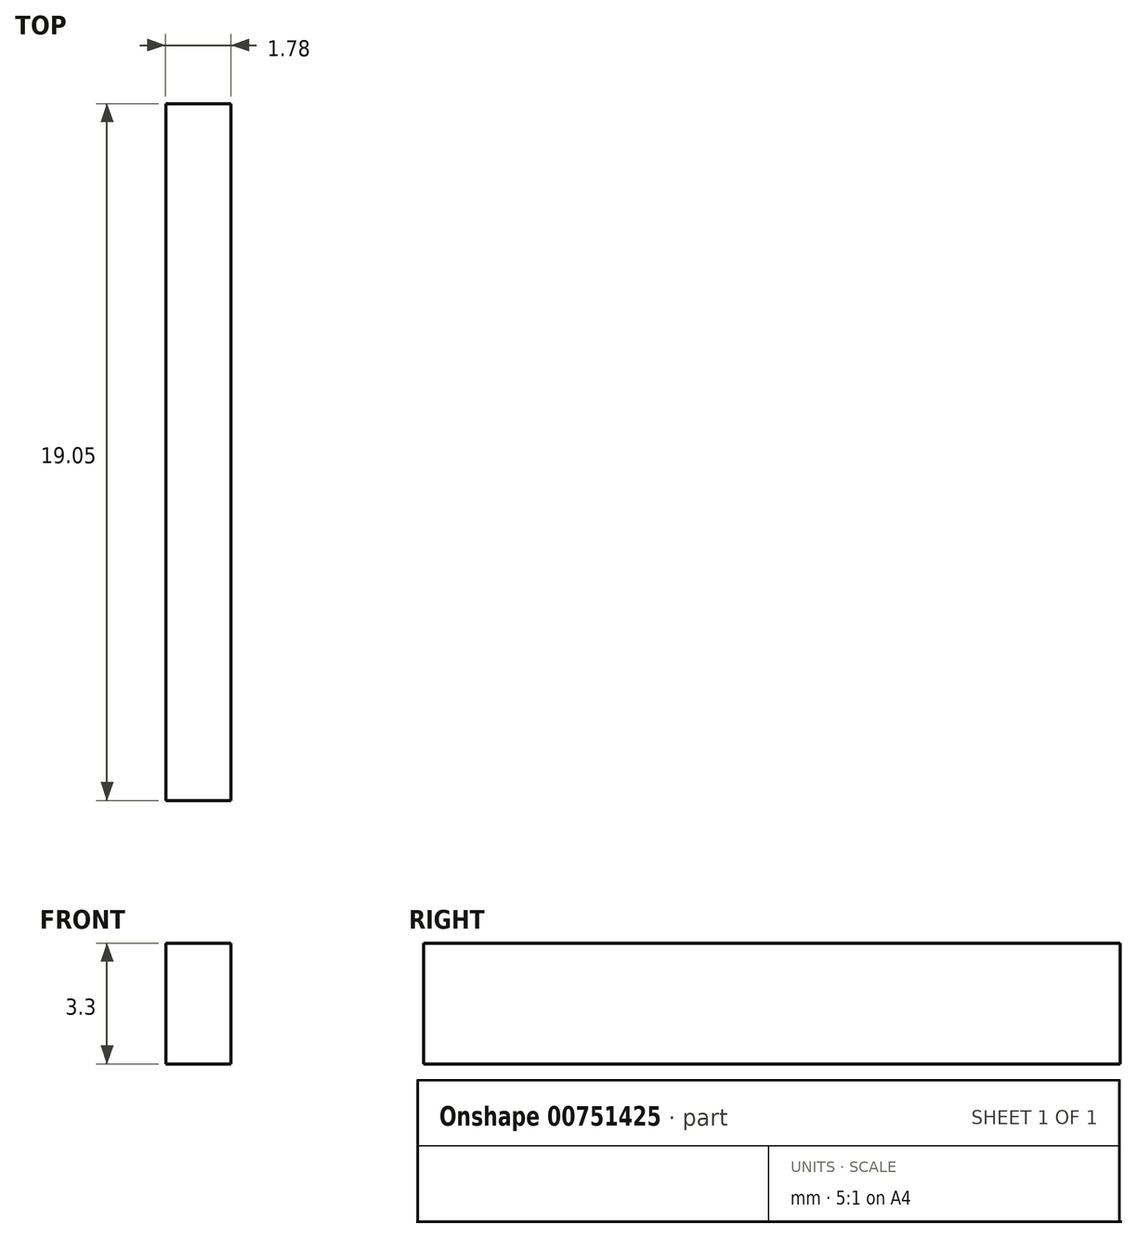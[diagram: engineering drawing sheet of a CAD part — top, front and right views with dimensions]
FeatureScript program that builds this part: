
annotation { "Feature Type Name" : "Feature", "Feature Type Description" : "" }
export const myFeature = defineFeature(function(context is Context, id is Id, definition is map)
    precondition{}
    {
        {
            var Q0;
            Q0=qCreatedBy(makeId("Top.planeOp"),FACE);
            var sketch = newSketch(context, id + "F0", { "sketchPlane" : qUnion([Q0])});
            skLineSegment(sketch, "E0.bottom", {"start": v(-1.78, 0) * mm, "end": v(0, 0) * mm});
            skLineSegment(sketch, "E0.top", {"start": v(-1.78, -19.05) * mm, "end": v(0, -19.05) * mm});
            skLineSegment(sketch, "E0.left", {"start": v(-1.78, 0) * mm, "end": v(-1.78, -19.05) * mm});
            skLineSegment(sketch, "E0.right", {"start": v(0, 0) * mm, "end": v(0, -19.05) * mm});
            skSolve(sketch);
        }
        {
            var Q0;
            Q0=makeQuery(id+"F0.imprint","IMPRINT",FACE,{"disambiguationData":[TD([[makeQuery(id+"F0.imprint","IMPRINT",EDGE,{"derivedFrom":sQuery(id+"F0.wireOp",EDGE,"E0.bottom")}),-1.0]])]});
            extrude(context, id + "F1", {"entities" : qUnion([Q0]), "depth" : 3.3 * mm, "offsetDistance" : 25.4 * mm});
        }
    });
